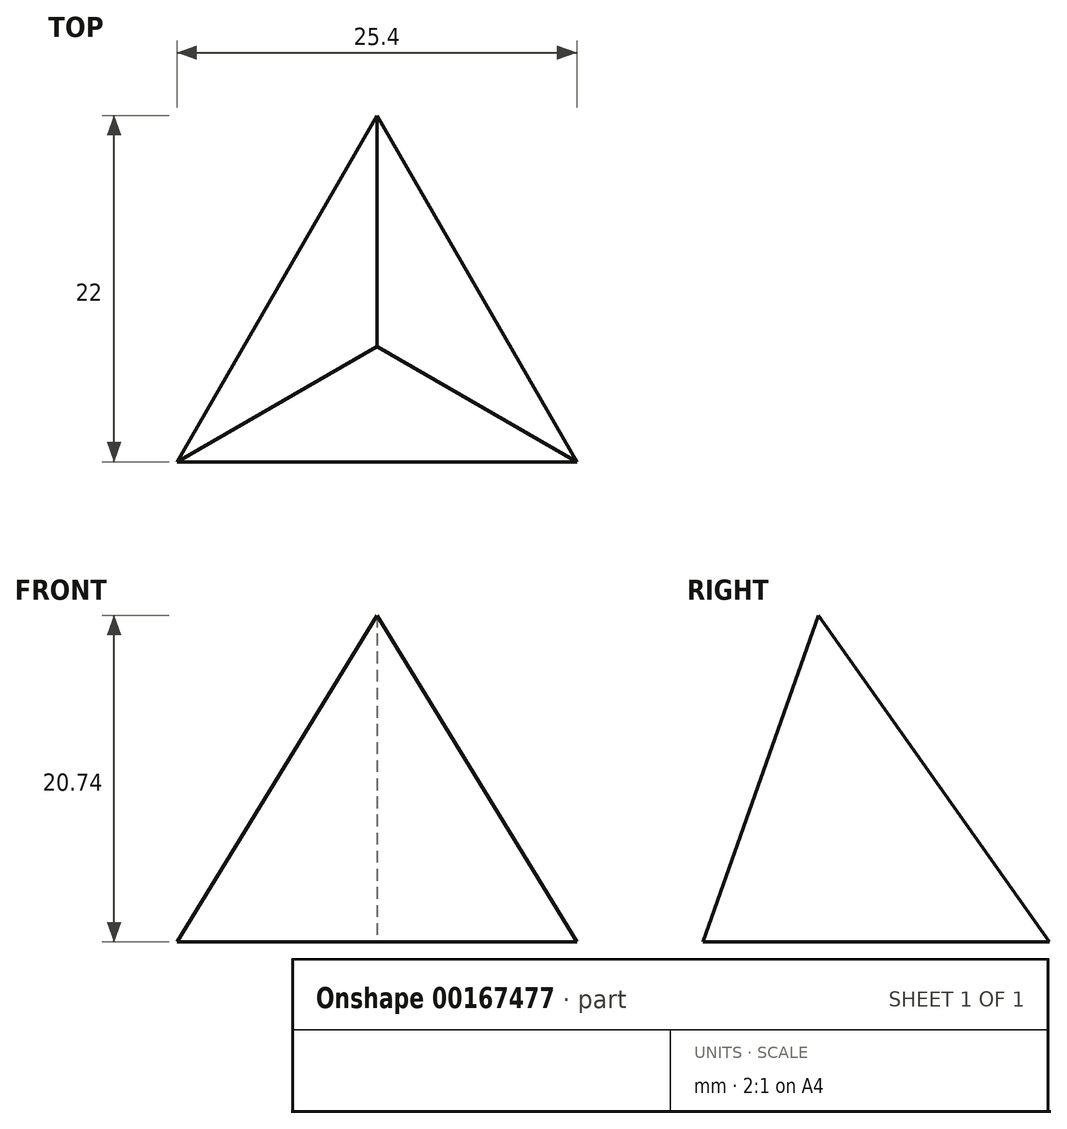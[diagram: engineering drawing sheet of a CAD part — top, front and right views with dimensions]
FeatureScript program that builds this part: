
annotation { "Feature Type Name" : "Feature", "Feature Type Description" : "" }
export const myFeature = defineFeature(function(context is Context, id is Id, definition is map)
    precondition{}
    {
        {
            var Q0;
            Q0=qCreatedBy(makeId("Top.planeOp"),FACE);
            var sketch = newSketch(context, id + "F0", { "sketchPlane" : qUnion([Q0])});
            skLineSegment(sketch, "E0", {"start": v(-12.7, 0) * mm, "end": v(0, 22) * mm});
            skLineSegment(sketch, "E1", {"start": v(0, 22) * mm, "end": v(12.7, 0) * mm});
            skLineSegment(sketch, "E2", {"start": v(12.7, 0) * mm, "end": v(-12.7, 0) * mm});
            skSolve(sketch);
        }
        {
            var Q0;
            Q0=makeQuery(id+"F0.imprint","IMPRINT",FACE,{"disambiguationData":[TD([[makeQuery(id+"F0.imprint","IMPRINT",EDGE,{"derivedFrom":sQuery(id+"F0.wireOp",EDGE,"E0")}),-1.0]])]});
            extrude(context, id + "F1", {"entities" : qUnion([Q0]), "depth" : 508 * mm, "hasDraft" : true, "draftAngle" : 90 * degree - atan(2 * (2 ^ 0.5)), "draftPullDirection" : true});
        }
    });
